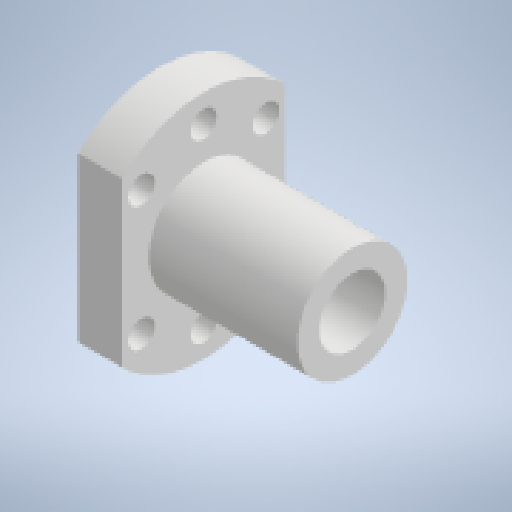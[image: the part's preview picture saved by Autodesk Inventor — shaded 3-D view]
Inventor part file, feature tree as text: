
AUTODESK INVENTOR PART (.ipt)
format: ipt  version: 2023 (Build 270158000, 158)  size: 169,984 bytes
history: native  units: mm
features: sketch x2, revolve x1, extrude x1
ambient origin geometry x8: Origin, YZ Plane, XZ Plane, XY Plane, X Axis, Y Axis, Z Axis, Center Point
bodies: Solid1 (feature_tree)
feature tree (4):
  revolve  "Revolution1"  [1 undecoded]
  extrude  "Extrusion1"  Depth=35.0mm
  sketch  "Sketch1"  dims[d0=10.0mm d1=21.0mm]
  sketch  "Sketch2"  dims[d2=8.0mm d3=35.0mm d4=6.0mm d5=90.0deg d6=45.0deg d7=32.0mm d8=4.8mm d10=10.0mm d11=0.0mm]
note: 1 required parameter value undecoded (feature->parameter linkage not recoverable at this tier; creation-order binding heuristic only, values carry confidence <= 0.55)
